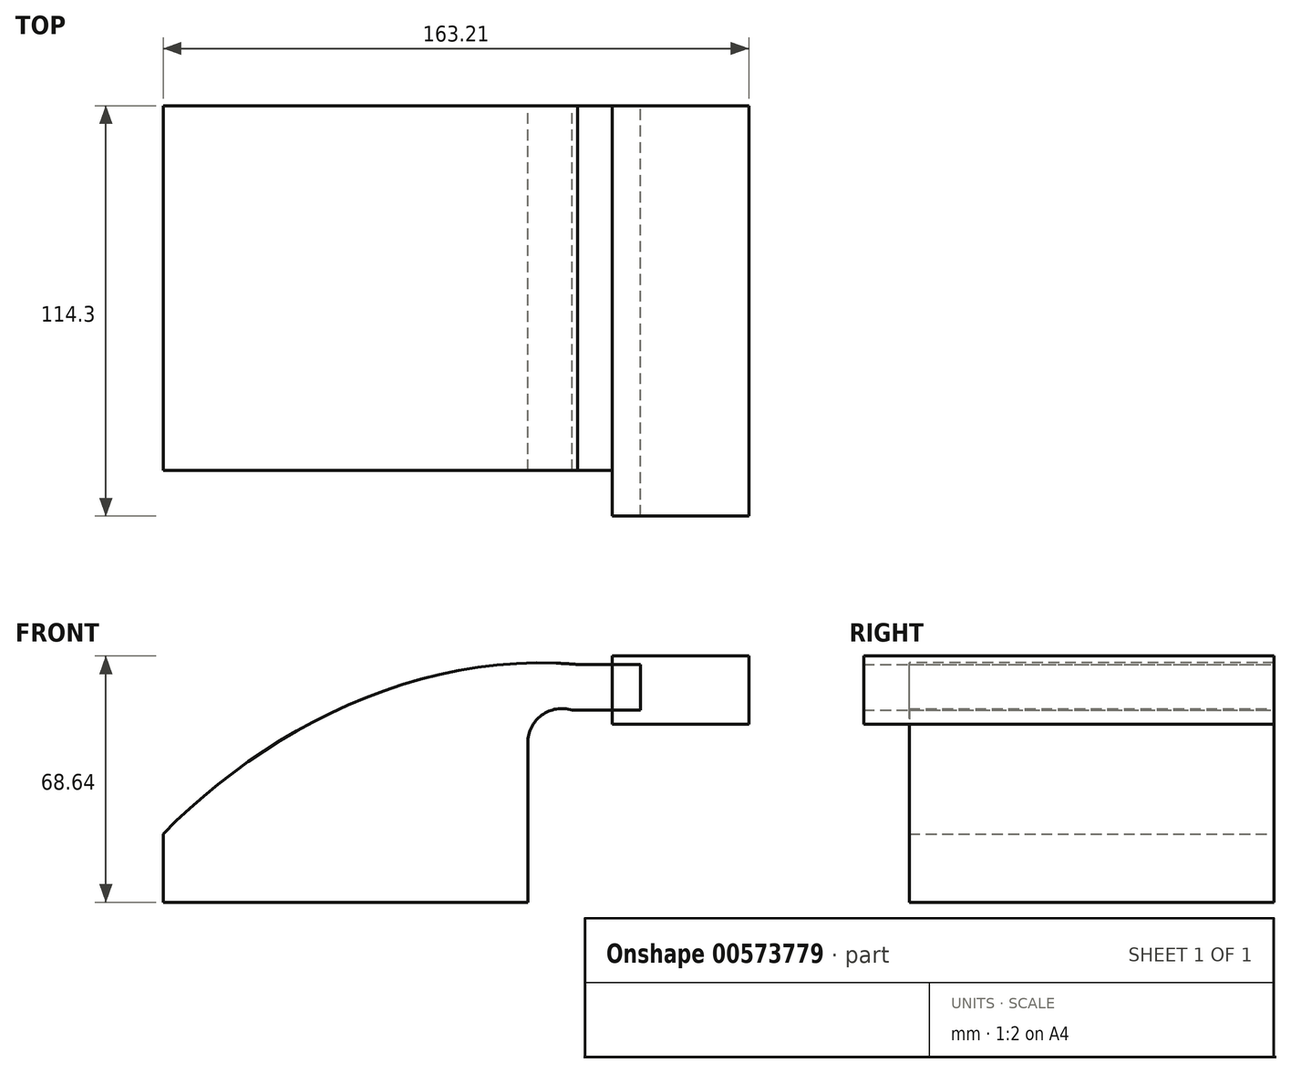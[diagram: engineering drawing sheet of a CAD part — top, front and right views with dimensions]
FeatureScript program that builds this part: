
annotation { "Feature Type Name" : "Feature", "Feature Type Description" : "" }
export const myFeature = defineFeature(function(context is Context, id is Id, definition is map)
    precondition{}
    {
        {
            var Q0;
            Q0=qCreatedBy(makeId("Front.planeOp"),FACE);
            var sketch = newSketch(context, id + "F0", { "sketchPlane" : qUnion([Q0])});
            skLineSegment(sketch, "E0.bottom", {"start": v(-50.8, -9.53) * mm, "end": v(50.8, -9.53) * mm});
            skLineSegment(sketch, "E0.top", {"start": v(-50.8, 9.53) * mm, "end": v(50.8, 9.53) * mm});
            skLineSegment(sketch, "E0.left", {"start": v(-50.8, -9.53) * mm, "end": v(-50.8, 9.53) * mm});
            skLineSegment(sketch, "E0.right", {"start": v(50.8, -9.53) * mm, "end": v(50.8, 9.53) * mm});
            skPoint(sketch, "E0.middle", {"position": v(0, 0) * mm});
            skLineSegment(sketch, "E1.bottom", {"start": v(74.31, 40.06) * mm, "end": v(112.41, 40.06) * mm});
            skLineSegment(sketch, "E1.top", {"start": v(74.31, 59.1) * mm, "end": v(112.41, 59.1) * mm});
            skLineSegment(sketch, "E1.left", {"start": v(74.31, 40.06) * mm, "end": v(74.31, 59.1) * mm});
            skLineSegment(sketch, "E1.right", {"start": v(112.41, 40.06) * mm, "end": v(112.41, 59.1) * mm});
            skPoint(sketch, "E1.middle", {"position": v(93.36, 49.58) * mm});
            skLineSegment(sketch, "E2", {"start": v(50.8, 9.53) * mm, "end": v(50.8, 34.92) * mm});
            skArc(sketch, "E3", {"start": v(50.8, 34.92) * mm, "mid": v(54.68, 42.6) * mm, "end": v(63.17, 44.02) * mm});
            skLineSegment(sketch, "E4", {"start": v(63.17, 44.02) * mm, "end": v(82.22, 44.02) * mm});
            skLineSegment(sketch, "E5.0", {"start": v(64.7, 56.72) * mm, "end": v(82.22, 56.72) * mm});
            skArc(sketch, "E5.1", {"start": v(38.1, 34.92) * mm, "mid": v(46.24, 52.12) * mm, "end": v(64.7, 56.72) * mm});
            skLineSegment(sketch, "E5.2", {"start": v(38.1, 9.53) * mm, "end": v(38.1, 34.92) * mm});
            skArc(sketch, "E6.0", {"start": v(57.15, 34.92) * mm, "mid": v(58.44, 37.48) * mm, "end": v(61.27, 37.96) * mm});
            skLineSegment(sketch, "E7", {"start": v(82.22, 44.02) * mm, "end": v(82.22, 56.72) * mm});
            skFitSpline(sketch, "E8", {"points": [v(-50.8, 9.53) * mm, v(64.7, 56.72) * mm], "startDerivative": vector(85.6, 86.86) * mm, "endDerivative": vector(134.35, -11.95) * mm});
            skSolve(sketch);
        }
        {
            var Q0;
            {var subQ3=sQuery(id+"F0.wireOp",EDGE,"E5.2");Q0=makeQuery(id+"F0.imprint","IMPRINT",FACE,{"disambiguationData":[TD([[makeQuery(id+"F0.imprint","IMPRINT",EDGE,{"derivedFrom":subQ3}),1.0]])]});}
            var Q1;
            Q1=makeQuery(id+"F0.imprint","IMPRINT",FACE,{"disambiguationData":[TD([[makeQuery(id+"F0.imprint","IMPRINT",EDGE,{"derivedFrom":sQuery(id+"F0.wireOp",EDGE,"E0.bottom")}),1.0]])]});
            var Q2;
            {var subQ0=sQuery(id+"F0.wireOp",EDGE,"E2");Q2=makeQuery(id+"F0.imprint","IMPRINT",FACE,{"disambiguationData":[TD([[makeQuery(id+"F0.imprint","IMPRINT",EDGE,{"derivedFrom":subQ0}),1.0]])]});}
            var Q3;
            {var subQ5=sQuery(id+"F0.wireOp",EDGE,"E1.bottom");Q3=makeQuery(id+"F0.imprint","IMPRINT",FACE,{"disambiguationData":[TD([[makeQuery(id+"F0.imprint","IMPRINT",EDGE,{"derivedFrom":subQ5}),1.0]])]});}
            extrude(context, id + "F1", {"entities" : qUnion([Q0, Q1, Q2, Q3]), "endBound" : BoundingType.SYMMETRIC, "depth" : 101.6 * mm, "offsetDistance" : 25.4 * mm});
        }
        {
            var Q0;
            Q0=makeQuery(id+"F1.opExtrude","CAP_FACE",FACE,{"disambiguationData":[OSD([sQuery(id+"F0.wireOp",EDGE,"E1.bottom"),sQuery(id+"F0.wireOp",EDGE,"E1.top"),sQuery(id+"F0.wireOp",EDGE,"E1.left"),sQuery(id+"F0.wireOp",EDGE,"E1.right"),sQuery(id+"F0.wireOp",EDGE,"E4"),sQuery(id+"F0.wireOp",EDGE,"E5.0"),sQuery(id+"F0.wireOp",EDGE,"E7")])],"isStart":false});
            extrude(context, id + "F2", {"entities" : qUnion([Q0]), "operationType" : NewBodyOperationType.ADD, "endBound" : BoundingType.SYMMETRIC, "depth" : 25.4 * mm, "offsetDistance" : 25.4 * mm});
        }
    });
